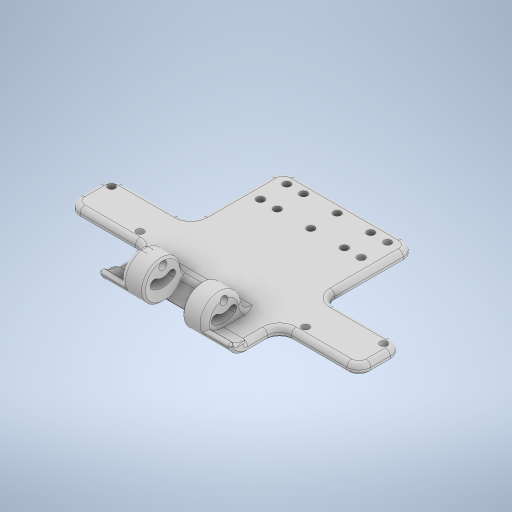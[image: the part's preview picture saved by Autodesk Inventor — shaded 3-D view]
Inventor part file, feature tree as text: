
AUTODESK INVENTOR PART (.ipt)
format: ipt  version: 2023 (Build 270158030, 158C)  size: 1,457,664 bytes
history: native  units: mm
features: fillet x26, extrude x20, sketch x19, projected_geometry x5, other x3, chamfer x3, mirror x2, plane x1
ambient origin geometry x8: Origin, YZ Plane, XZ Plane, XY Plane, X Axis, Y Axis, Z Axis, Center Point
bodies: Body1 (feature_tree), Body2 (feature_tree), Body3 (feature_tree)
feature tree (79):
  other  "Ping Sensor Base"
  extrude  "Extrusion1"  Depth=3.0mm TaperAngle=0.0deg
  extrude  "Extrusion2"  Depth=3.0mm TaperAngle=0.0deg
  extrude  "Extrusion3"  Depth=1.55mm
  fillet  "Fillet1"  Radius=12.0mm
  extrude  "Extrusion4"  Depth=14.0mm
  extrude  "Extrusion6"  Depth=1.5mm
  fillet  "Fillet9"  Radius=7.0mm
  fillet  "Fillet10"  Radius=7.0mm
  fillet  "Fillet11"  [1 undecoded]
  fillet  "Fillet12"  Radius=15.0mm
  fillet  "Fillet15"  Radius=6.0mm
  fillet  "Fillet16"  Radius=15.0mm
  extrude  "Extrusion7"  Depth=30.0mm
  extrude  "Extrusion8"  Depth=3.1mm
  extrude  "Extrusion9"  Depth=3.0mm
  extrude  "Extrusion10"  Depth=8.2mm
  fillet  "Fillet17"  Radius=10.2mm
  fillet  "Fillet18"  Radius=8.2mm
  fillet  "Fillet19"  Radius=10.2mm
  fillet  "Fillet20"  Radius=7.5mm
  fillet  "Fillet21"  Radius=7.5mm
  fillet  "Fillet22"  [1 undecoded]
  extrude  "Extrusion11"  Depth=7.0mm
  fillet  "Fillet27"  Radius=2.0mm
  extrude  "Extrusion13"  Depth=2.0mm
  fillet  "Fillet29"  Radius=3.0mm
  fillet  "Fillet30"  Radius=17.0mm
  fillet  "Fillet31"  Radius=26.0mm
  fillet  "Fillet32"  Radius=10.0mm
  fillet  "Fillet33"  Radius=27.0mm
  extrude  "Extrusion14"  Depth=26.0mm
  mirror  "Mirror1"
  extrude  "Extrusion15"  Depth=45.8mm
  fillet  "Fillet34"  Radius=20.8mm
  extrude  "Extrusion17"  Depth=3.1mm
  mirror  "Mirror2"
  fillet  "Fillet35"  Radius=3.1mm
  fillet  "Fillet36"  Radius=3.1mm
  fillet  "Fillet39"  Radius=5.5mm
  plane  "Work Plane4"
  extrude  "Extrusion18"  Depth=17.0mm
  extrude  "Extrusion19"  Depth=9.75mm
  chamfer  "Chamfer1"  Distance=9.3mm
  chamfer  "Chamfer2"  [1 undecoded]
  fillet  "Fillet40"  Radius=8.0mm
  extrude  "Extrusion20"  Depth=4.5mm
  extrude  "Extrusion21"  Depth=2.0mm
  extrude  "Extrusion22"  Depth=7.0mm
  extrude  "Extrusion23"  Depth=3.0mm
  fillet  "Fillet41"  Radius=1.0mm
  chamfer  "Chamfer4"  Distance=3.1mm
  fillet  "Fillet42"  Radius=3.1mm
  sketch  "Sketch1"  dims[d0=36.0mm d1=3.0mm d2=0.0mm]
  sketch  "Sketch2"  dims[d3=3.1mm d4=3.0mm d5=0.0mm]
  sketch  "Sketch3"  dims[d7=3.1mm d8=1.55mm d9=12.0mm]
  sketch  "Sketch4"  dims[d10=3.0mm d11=0.0mm d15=14.0mm]
  sketch  "Sketch6"  dims[d16=3.5mm d17=1.5mm]
  sketch  "Sketch7"  dims[d18=2.5mm d19=6.5mm d20=20.0mm d21=0.0mm d22=7.0mm d23=7.0mm d24=0.0mm d25=15.0mm d37=6.0mm d54=15.0mm]
  other  "Ping Sensor Housing"
  sketch  "Sketch8"  dims[d55=15.0mm d56=30.0mm]
  sketch  "Sketch9"  dims[d57=3.0mm d58=3.1mm]
  sketch  "Sketch10"  dims[d59=4.5mm d60=3.0mm]
  sketch  "Sketch11"  dims[d61=3.1mm d62=8.2mm d63=10.2mm d64=8.2mm d65=10.2mm d66=7.5mm d67=7.5mm d68=0.0mm d69=0.0mm]
  sketch  "Sketch13"  dims[d70=1.5mm d71=7.0mm d72=2.0mm]
  sketch  "Sketch14"  dims[d73=1.0mm d76=2.0mm d77=3.0mm d78=17.0mm d79=26.0mm d80=10.0mm d81=0.0mm d82=27.0mm]
  projected_geometry  "Projected Loop1"
  projected_geometry  "Projected Loop2"
  other  "hoz-mount"
  sketch  "Sketch15"  dims[d83=26.0mm d84=26.0mm]
  projected_geometry  "Projected Loop3"
  sketch  "Sketch17"  dims[d85=10.0mm d86=0.0mm d87=45.8mm d88=20.8mm]
  projected_geometry  "Projected Loop7"
  sketch  "Sketch19"  dims[d89=3.1mm d90=3.1mm d91=3.1mm d92=3.1mm d93=5.5mm d94=0.0mm]
  sketch  "Sketch20"  dims[d95=17.0mm d96=17.0mm]
  sketch  "Sketch21"  dims[d97=9.75mm d99=9.75mm]
  sketch  "Sketch22"  dims[d100=10.0mm]
  sketch  "Sketch23"  dims[d101=10.0mm d102=9.3mm d103=0.0mm d104=0.0mm d105=8.0mm d106=4.5mm d107=2.0mm d108=7.0mm d109=3.0mm d110=1.0mm d111=3.1mm d112=3.1mm d113=6.1mm d114=0.0mm d115=0.0mm d116=4.0mm d118=4.0mm d135=0.9mm d137=0.0mm d138=6.0mm d139=5.0mm d140=5.0mm d141=4.0mm d142=3.0mm d143=0.0mm d144=1.0mm d145=0.3mm d146=1.0mm d147=26.3mm d148=43.3mm d149=1.0mm d150=1.0mm d160=1.0mm d161=67.7mm d162=4.0mm d163=6.0mm d164=3.5mm d165=3.5mm d166=0.1mm d167=0.2mm d168=19.5mm d169=0.0mm d170=10.0mm d171=0.0mm d172=2.0mm d177=10.0mm d178=0.0mm d179=2.0mm d180=1.0mm d183=2.0mm d185=42.0mm d188=3.1mm d189=0.0mm d190=0.0mm d191=4.75mm d192=4.0mm d193=0.0mm d194=2.0mm d195=2.0mm d196=45.0deg d197=0.8mm d198=2.0mm d199=45.0deg d203=0.3mm d204=33.1mm d205=33.1mm d206=20.47mm d208=10.0mm d209=0.0mm d210=3.0mm d211=10.3mm d212=22.2mm d213=22.2mm d214=3.9mm d215=3.877918mm d216=3.9mm d217=3.9mm d218=0.0mm d219=0.0mm d220=3.0mm d223=27.5mm d224=55.0mm d225=14.0mm d226=14.0mm d227=6.5mm d228=6.5mm d229=28.49mm d230=6.0mm d231=0.0mm d232=0.0mm d233=10.0mm d234=5.0mm d235=10.0mm d236=0.0mm d237=5.0mm d238=1.0mm d239=2.0mm d240=45.0deg d241=2.0mm]
  projected_geometry  "Projected Loop8"
note: 3 required parameter values undecoded (feature->parameter linkage not recoverable at this tier; creation-order binding heuristic only, values carry confidence <= 0.55)
